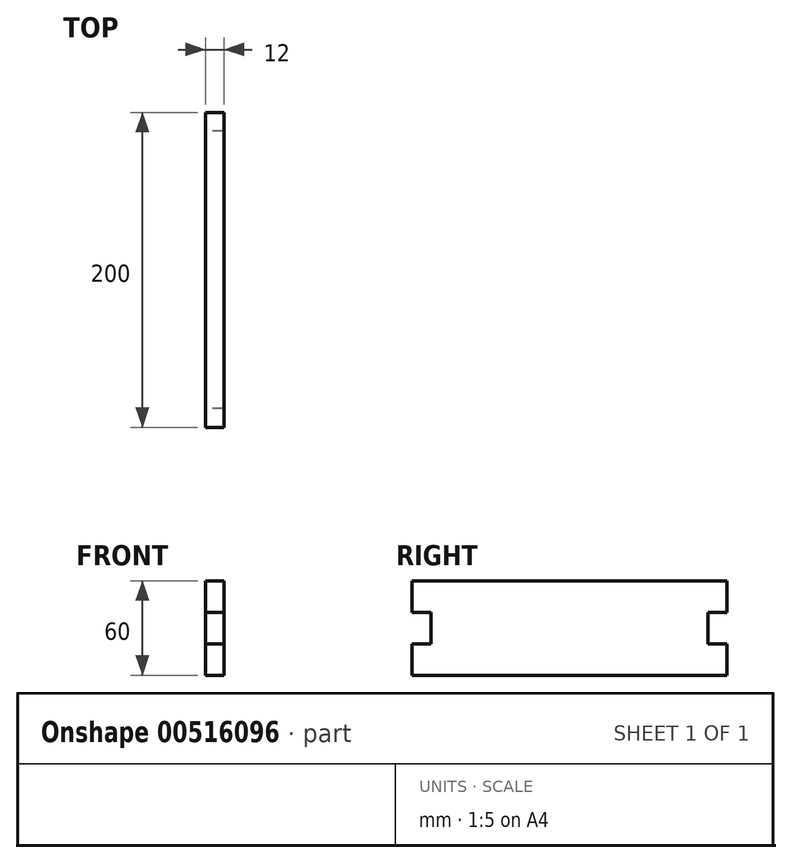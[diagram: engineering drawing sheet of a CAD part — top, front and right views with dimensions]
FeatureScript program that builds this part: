
annotation { "Feature Type Name" : "Feature", "Feature Type Description" : "" }
export const myFeature = defineFeature(function(context is Context, id is Id, definition is map)
    precondition{}
    {
        {
            var Q0;
            Q0=qCreatedBy(makeId("Right.planeOp"),FACE);
            var sketch = newSketch(context, id + "F0", { "sketchPlane" : qUnion([Q0])});
            skLineSegment(sketch, "E0", {"start": v(0, 0) * mm, "end": v(0, 20) * mm});
            skLineSegment(sketch, "E1", {"start": v(0, 20) * mm, "end": v(12, 20) * mm});
            skLineSegment(sketch, "E2", {"start": v(12, 20) * mm, "end": v(12, 40) * mm});
            skLineSegment(sketch, "E3", {"start": v(12, 40) * mm, "end": v(0, 40) * mm});
            skLineSegment(sketch, "E4", {"start": v(0, 40) * mm, "end": v(0, 60) * mm});
            skLineSegment(sketch, "E5", {"start": v(0, 60) * mm, "end": v(100, 60) * mm});
            skLineSegment(sketch, "E6", {"start": v(100, 60) * mm, "end": v(100, 0) * mm, "construction": true});
            skLineSegment(sketch, "E7", {"start": v(100, 0) * mm, "end": v(0, 0) * mm});
            skLineSegment(sketch, "E8.MirrorCS", {"start": v(200, 20) * mm, "end": v(188, 20) * mm});
            skLineSegment(sketch, "E9.MirrorCS", {"start": v(188, 20) * mm, "end": v(188, 40) * mm});
            skLineSegment(sketch, "E10.MirrorCS", {"start": v(188, 40) * mm, "end": v(200, 40) * mm});
            skLineSegment(sketch, "E11.MirrorCS", {"start": v(200, 60) * mm, "end": v(100, 60) * mm});
            skLineSegment(sketch, "E12.MirrorCS", {"start": v(200, 0) * mm, "end": v(200, 20) * mm});
            skLineSegment(sketch, "E13.MirrorCS", {"start": v(200, 40) * mm, "end": v(200, 60) * mm});
            skLineSegment(sketch, "E14.MirrorCS", {"start": v(100, 0) * mm, "end": v(200, 0) * mm});
            skSolve(sketch);
        }
        {
            var Q0;
            Q0 = qSketchRegion(id + "F0", true);
            extrude(context, id + "F1", {"entities" : qUnion([Q0]), "depth" : 12 * mm, "offsetDistance" : 25.4 * mm});
        }
    });
